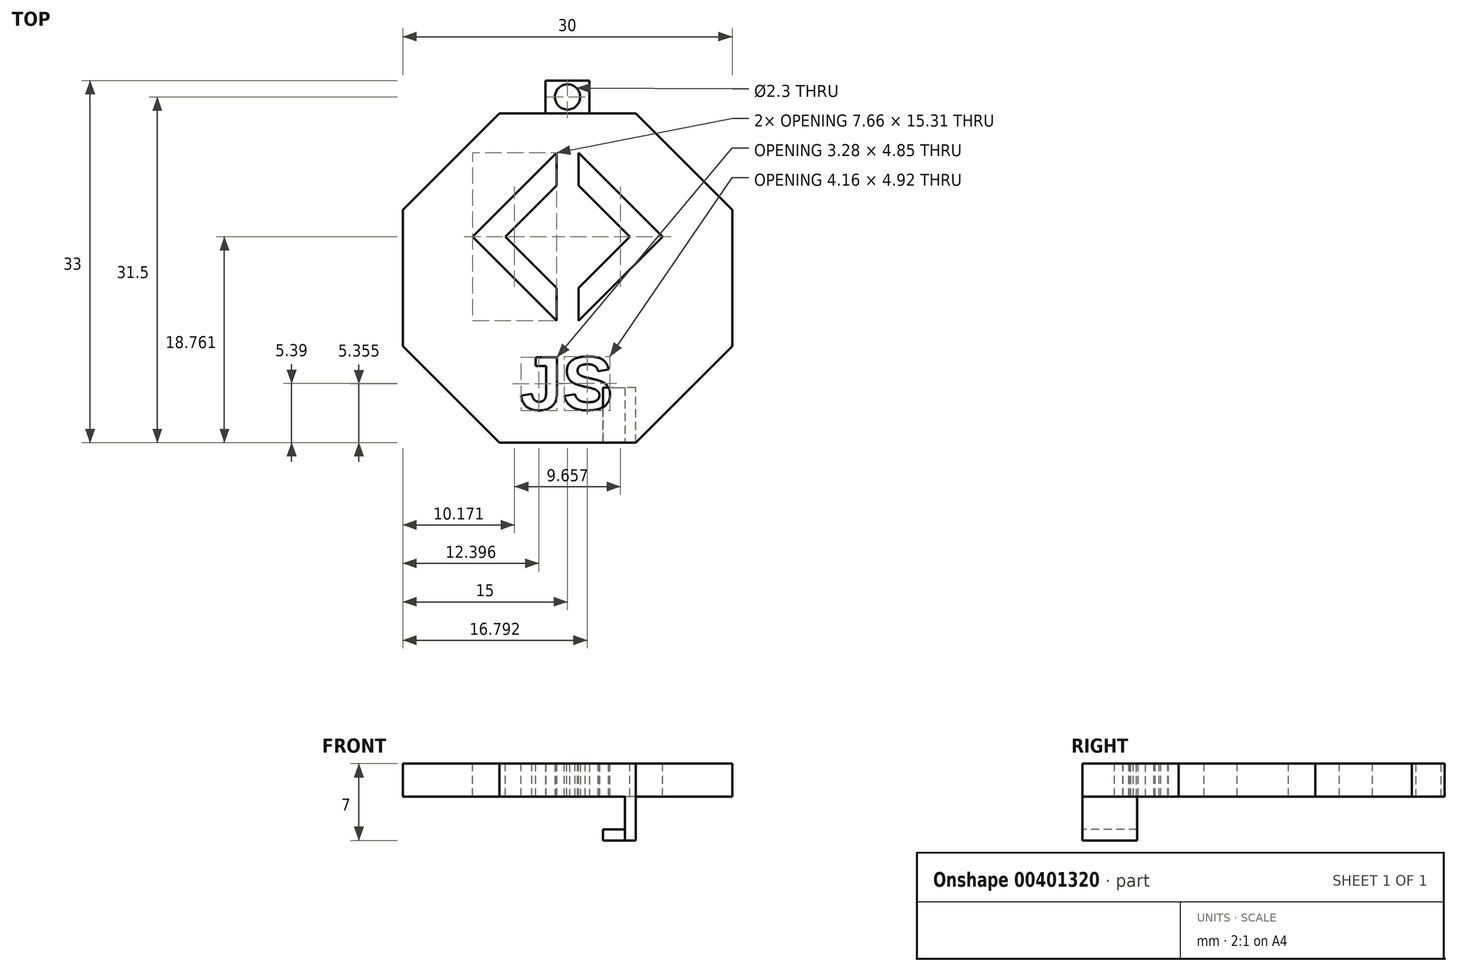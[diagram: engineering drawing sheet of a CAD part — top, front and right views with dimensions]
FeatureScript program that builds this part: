
annotation { "Feature Type Name" : "Feature", "Feature Type Description" : "" }
export const myFeature = defineFeature(function(context is Context, id is Id, definition is map)
    precondition{}
    {
        {
            var Q0;
            Q0=qCreatedBy(makeId("Top.planeOp"),FACE);
            var sketch = newSketch(context, id + "F0", { "sketchPlane" : qUnion([Q0])});
            skCircle(sketch, "E0.cCircle", {"center": v(0, 0) * mm, "radius": 15 * mm, "construction": true});
            skLineSegment(sketch, "E0.0", {"start": v(15, 6.21) * mm, "end": v(15, -6.21) * mm});
            skLineSegment(sketch, "E0.1", {"start": v(15, -6.21) * mm, "end": v(6.21, -15) * mm});
            skLineSegment(sketch, "E0.2", {"start": v(6.21, -15) * mm, "end": v(-6.21, -15) * mm});
            skLineSegment(sketch, "E0.3", {"start": v(-6.21, -15) * mm, "end": v(-15, -6.21) * mm});
            skLineSegment(sketch, "E0.4", {"start": v(-15, -6.21) * mm, "end": v(-15, 6.21) * mm});
            skLineSegment(sketch, "E0.5", {"start": v(-15, 6.21) * mm, "end": v(-6.21, 15) * mm});
            skLineSegment(sketch, "E0.6", {"start": v(-6.21, 15) * mm, "end": v(6.21, 15) * mm});
            skLineSegment(sketch, "E0.7", {"start": v(6.21, 15) * mm, "end": v(15, 6.21) * mm});
            skPoint(sketch, "E0.0.midPoint", {"position": v(15, 0) * mm});
            skLineSegment(sketch, "E1", {"start": v(0, 0) * mm, "end": v(-15, 0) * mm, "construction": true});
            skSolve(sketch);
        }
        {
            var Q0;
            Q0=qSketchRegion(id+"F0",true);
            extrude(context, id + "F1", {"entities" : qUnion([Q0]), "depth" : 3 * mm});
        }
        {
            var Q0;
            Q0=makeQuery(id+"F1.opExtrude","CAP_FACE",FACE,{"disambiguationData":[OSD([sQuery(id+"F0.wireOp",EDGE,"E0.0"),sQuery(id+"F0.wireOp",EDGE,"E0.1"),sQuery(id+"F0.wireOp",EDGE,"E0.2"),sQuery(id+"F0.wireOp",EDGE,"E0.3"),sQuery(id+"F0.wireOp",EDGE,"E0.4"),sQuery(id+"F0.wireOp",EDGE,"E0.5"),sQuery(id+"F0.wireOp",EDGE,"E0.6"),sQuery(id+"F0.wireOp",EDGE,"E0.7")])],"isStart":false});
            var sketch = newSketch(context, id + "F2", { "sketchPlane" : qUnion([Q0])});
            skText(sketch, "E2", { "text": "JS", "fontName": "Arimo-Bold.ttf"});
            skArc(sketch, "E3.cCircle", {"start": v(2.83, 0.93) * mm, "mid": v(0, 7.76) * mm, "end": v(-2.83, 0.93) * mm, "construction": true});
            skLineSegment(sketch, "E3.0", {"start": v(5.66, 3.76) * mm, "end": v(1, -0.9) * mm});
            skLineSegment(sketch, "E3.2", {"start": v(-5.66, 3.76) * mm, "end": v(-1, 8.42) * mm});
            skLineSegment(sketch, "E3.3", {"start": v(1, 8.42) * mm, "end": v(5.66, 3.76) * mm});
            skPoint(sketch, "E3.0.midPoint", {"position": v(2.83, 0.93) * mm});
            skLineSegment(sketch, "E4", {"start": v(-5.66, 3.76) * mm, "end": v(0, 3.76) * mm, "construction": true});
            skLineSegment(sketch, "E5.1", {"start": v(8.66, 3.76) * mm, "end": v(1, -3.9) * mm});
            skLineSegment(sketch, "E5.3", {"start": v(-8.66, 3.76) * mm, "end": v(-1, 11.42) * mm});
            skPoint(sketch, "E5.0.midPoint", {"position": v(4.33, 8.1) * mm});
            skLineSegment(sketch, "E6", {"start": v(-8.66, 3.76) * mm, "end": v(-5.66, 3.76) * mm, "construction": true});
            skPoint(sketch, "E7.orphan", {"position": v(0, -1.9) * mm});
            skPoint(sketch, "E8.orphan", {"position": v(0, -4.9) * mm});
            skPoint(sketch, "E9.orphan", {"position": v(0.45, -660.17) * mm});
            skPoint(sketch, "E10.orphan", {"position": v(-0.45, -23.95) * mm});
            skLineSegment(sketch, "E11.trimOffspring", {"start": v(0, 3.76) * mm, "end": v(8.66, 3.76) * mm, "construction": true});
            skPoint(sketch, "E12.orphan", {"position": v(0, 9.42) * mm});
            skPoint(sketch, "E13.orphan", {"position": v(0, 12.42) * mm});
            skPoint(sketch, "E14.bottom.end.orphan", {"position": v(0.45, 31.48) * mm});
            skPoint(sketch, "E14.bottom.start.orphan", {"position": v(-0.45, 667.69) * mm});
            skPoint(sketch, "E15.firstSnap0", {"position": v(-10.6, -10.6) * mm});
            skPoint(sketch, "E15.secondSnap0", {"position": v(10.6, 10.6) * mm});
            skPoint(sketch, "E16.startSnap0", {"position": v(0.45, 11.37) * mm});
            skLineSegment(sketch, "E17", {"start": v(1, 11.42) * mm, "end": v(1, 8.42) * mm});
            skLineSegment(sketch, "E18", {"start": v(-1, 11.42) * mm, "end": v(-1, 8.42) * mm});
            skPoint(sketch, "E19.orphan", {"position": v(0.45, 12.87) * mm});
            skLineSegment(sketch, "E20.trimOffspring", {"start": v(1, 11.42) * mm, "end": v(8.66, 3.76) * mm});
            skPoint(sketch, "E21.trimOffspring.end.orphan", {"position": v(0.45, 9.87) * mm});
            skLineSegment(sketch, "E22.trimOffspring", {"start": v(-1, -0.9) * mm, "end": v(-5.66, 3.76) * mm});
            skLineSegment(sketch, "E23.trimOffspring", {"start": v(-1, -0.9) * mm, "end": v(-1, -3.9) * mm});
            skLineSegment(sketch, "E24.trimOffspring", {"start": v(1, -0.9) * mm, "end": v(1, -3.9) * mm});
            skLineSegment(sketch, "E25.trimOffspring", {"start": v(-1, -3.9) * mm, "end": v(-8.66, 3.76) * mm});
            const initialGuessF2  = {"E2": [-0.00435, -0.012, 1, 0, 0.005]};
            skSetInitialGuess(sketch, initialGuessF2);
            skSolve(sketch);
        }
        {
            var Q0;
            Q0=qSketchRegion(id+"F2",true);
            extrude(context, id + "F3", {"entities" : qUnion([Q0]), "operationType" : NewBodyOperationType.REMOVE, "endBound" : BoundingType.THROUGH_ALL, "oppositeDirection" : true, "depth" : 3 * mm});
        }
        {
            var Q0;
            Q0=makeQuery(id+"F1.opExtrude","CAP_FACE",FACE,{"disambiguationData":[OSD([sQuery(id+"F0.wireOp",EDGE,"E0.0"),sQuery(id+"F0.wireOp",EDGE,"E0.1"),sQuery(id+"F0.wireOp",EDGE,"E0.2"),sQuery(id+"F0.wireOp",EDGE,"E0.3"),sQuery(id+"F0.wireOp",EDGE,"E0.4"),sQuery(id+"F0.wireOp",EDGE,"E0.5"),sQuery(id+"F0.wireOp",EDGE,"E0.6"),sQuery(id+"F0.wireOp",EDGE,"E0.7")])],"isStart":true});
            var sketch = newSketch(context, id + "F4", { "sketchPlane" : qUnion([Q0])});
            skLineSegment(sketch, "E26.bottom", {"start": v(6.21, 15) * mm, "end": v(5.21, 15) * mm});
            skLineSegment(sketch, "E26.top", {"start": v(6.21, 10) * mm, "end": v(5.21, 10) * mm});
            skLineSegment(sketch, "E26.left", {"start": v(6.21, 15) * mm, "end": v(6.21, 10) * mm});
            skLineSegment(sketch, "E26.right", {"start": v(5.21, 15) * mm, "end": v(5.21, 10) * mm});
            skSolve(sketch);
        }
        {
            var Q0;
            Q0=qSketchRegion(id+"F4",true);
            extrude(context, id + "F5", {"entities" : qUnion([Q0]), "operationType" : NewBodyOperationType.ADD, "depth" : 4 * mm});
        }
        {
            var Q0;
            Q0=makeQuery(id+"F5.opExtrude","SWEPT_FACE",FACE,{"disambiguationData":[OSD([sQuery(id+"F4.wireOp",EDGE,"E26.right")])]});
            var sketch = newSketch(context, id + "F6", { "sketchPlane" : qUnion([Q0])});
            skLineSegment(sketch, "E27.bottom", {"start": v(10, -4) * mm, "end": v(15, -4) * mm});
            skLineSegment(sketch, "E27.top", {"start": v(10, -3) * mm, "end": v(15, -3) * mm});
            skLineSegment(sketch, "E27.left", {"start": v(10, -4) * mm, "end": v(10, -3) * mm});
            skLineSegment(sketch, "E27.right", {"start": v(15, -4) * mm, "end": v(15, -3) * mm});
            skSolve(sketch);
        }
        {
            var Q0;
            Q0=makeQuery(id+"F6.imprint","IMPRINT",FACE,{"disambiguationData":[TD([[makeQuery(id+"F6.imprint","IMPRINT",EDGE,{"derivedFrom":sQuery(id+"F6.wireOp",EDGE,"E27.bottom")}),-1.0]])]});
            var Q1;
            Q1=sQuery(id+"F6.wireOp",EDGE,"E27.top");
            var Q2;
            Q2=sQuery(id+"F6.wireOp",EDGE,"E27.bottom");
            var Q3;
            Q3=sQuery(id+"F6.wireOp",EDGE,"E27.right");
            var Q4;
            Q4=sQuery(id+"F6.wireOp",EDGE,"E27.left");
            extrude(context, id + "F7", {"entities" : qUnion([Q0]), "surfaceEntities" : qUnion([Q1, Q2, Q3, Q4]), "depth" : 2 * mm});
        }
        {
            var Q0;
            Q0=makeQuery(id+"F1.opExtrude","SWEPT_FACE",FACE,{"disambiguationData":[OSD([sQuery(id+"F0.wireOp",EDGE,"E0.6")])]});
            var sketch = newSketch(context, id + "F8", { "sketchPlane" : qUnion([Q0])});
            skLineSegment(sketch, "E28.bottom", {"start": v(2, 3) * mm, "end": v(-2, 3) * mm});
            skLineSegment(sketch, "E28.top", {"start": v(2, 0) * mm, "end": v(-2, 0) * mm});
            skLineSegment(sketch, "E28.left", {"start": v(2, 3) * mm, "end": v(2, 0) * mm});
            skLineSegment(sketch, "E28.right", {"start": v(-2, 3) * mm, "end": v(-2, 0) * mm});
            skPoint(sketch, "E28.middle", {"position": v(0, 1.5) * mm});
            skPoint(sketch, "E28.middle.positionSnap0", {"position": v(0, 3) * mm});
            skPoint(sketch, "E28.centerSnap0", {"position": v(0, 3) * mm});
            skSolve(sketch);
        }
        {
            var Q0;
            Q0=qSketchRegion(id+"F8",true);
            extrude(context, id + "F9", {"entities" : qUnion([Q0]), "depth" : 3 * mm});
        }
        {
            var Q0;
            Q0=makeQuery(id+"F9.opExtrude","SWEPT_FACE",FACE,{"disambiguationData":[OSD([sQuery(id+"F8.wireOp",EDGE,"E28.top")])]});
            var sketch = newSketch(context, id + "F10", { "sketchPlane" : qUnion([Q0])});
            skCircle(sketch, "E29", {"center": v(0, -16.5) * mm, "radius": 1.15 * mm});
            skLineSegment(sketch, "E30", {"start": v(0, -16.5) * mm, "end": v(0, -15) * mm, "construction": true});
            skLineSegment(sketch, "E31", {"start": v(0, -16.5) * mm, "end": v(0, -18) * mm, "construction": true});
            skSolve(sketch);
        }
        {
            var Q0;
            Q0=qSketchRegion(id+"F10",true);
            extrude(context, id + "F11", {"entities" : qUnion([Q0]), "operationType" : NewBodyOperationType.REMOVE, "endBound" : BoundingType.THROUGH_ALL, "oppositeDirection" : true, "depth" : 25 * mm});
        }
    });
